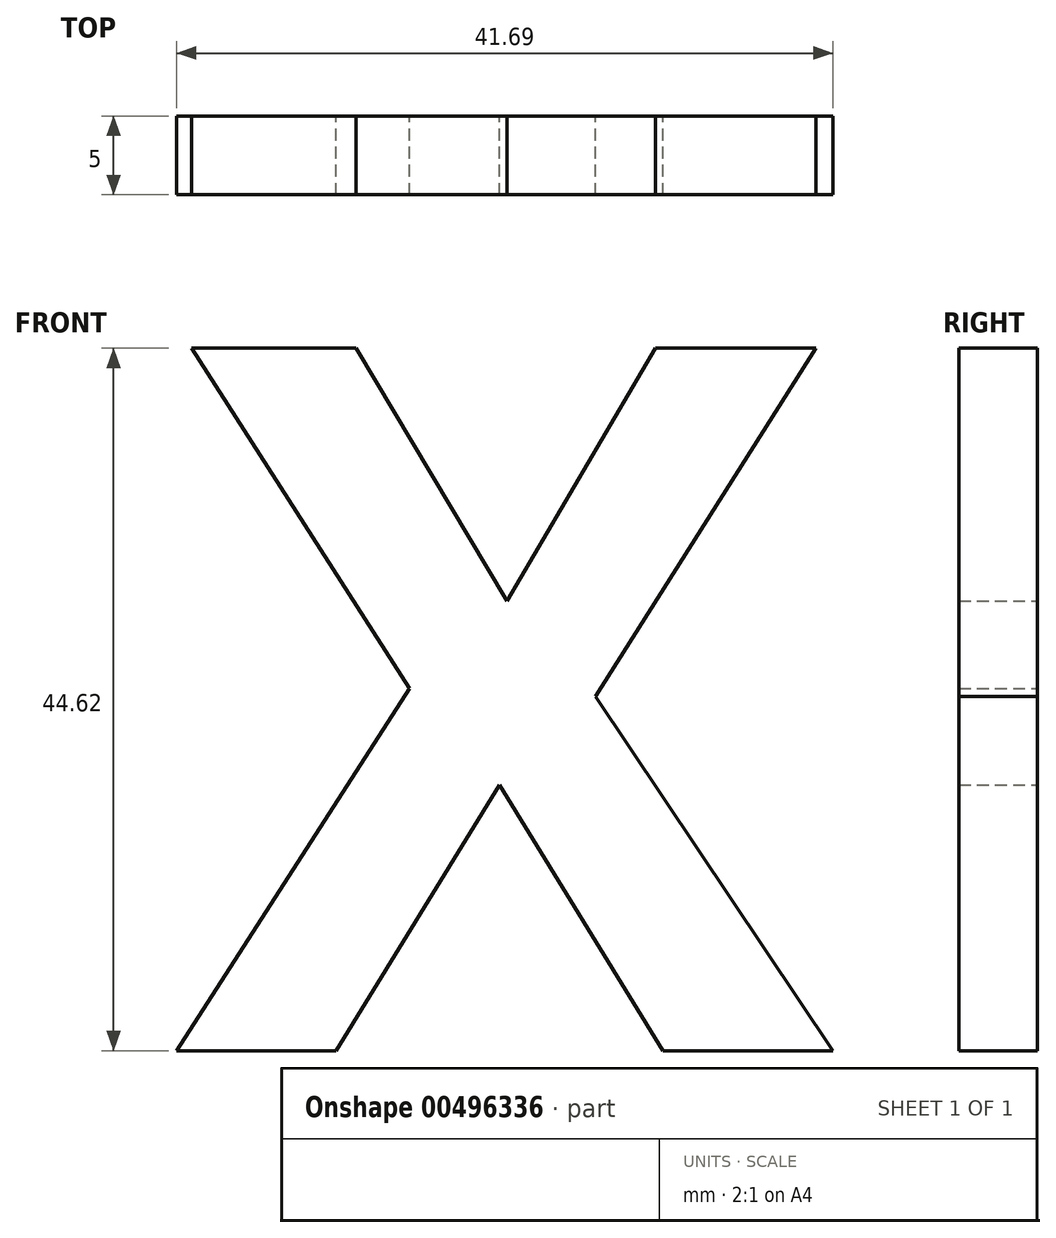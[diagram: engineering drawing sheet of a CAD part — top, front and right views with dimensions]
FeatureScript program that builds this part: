
annotation { "Feature Type Name" : "Feature", "Feature Type Description" : "" }
export const myFeature = defineFeature(function(context is Context, id is Id, definition is map)
    precondition{}
    {
        {
            var Q0;
            Q0=qCreatedBy(makeId("Front.planeOp"),FACE);
            var sketch = newSketch(context, id + "F0", { "sketchPlane" : qUnion([Q0])});
            skText(sketch, "E0", { "text": "X", "fontName": "OpenSans-Bold.ttf"});
            const initialGuessF0  = {"E0": [-0.06278, 0.02008, 1, 0, 0.045]};
            skSetInitialGuess(sketch, initialGuessF0);
            skSolve(sketch);
        }
        {
            var Q0;
            Q0=makeQuery(id+"F0.imprint","IMPRINT",FACE,{"disambiguationData":[TD([[makeQuery(id+"F0.imprint","IMPRINT",EDGE,{"derivedFrom":sQuery(id+"F0.wireOp",EDGE,"E0.sketch_text.stroke-0")}),-1.0]])]});
            extrude(context, id + "F1", {"entities" : qUnion([Q0]), "depth" : 5 * mm});
        }
    });
